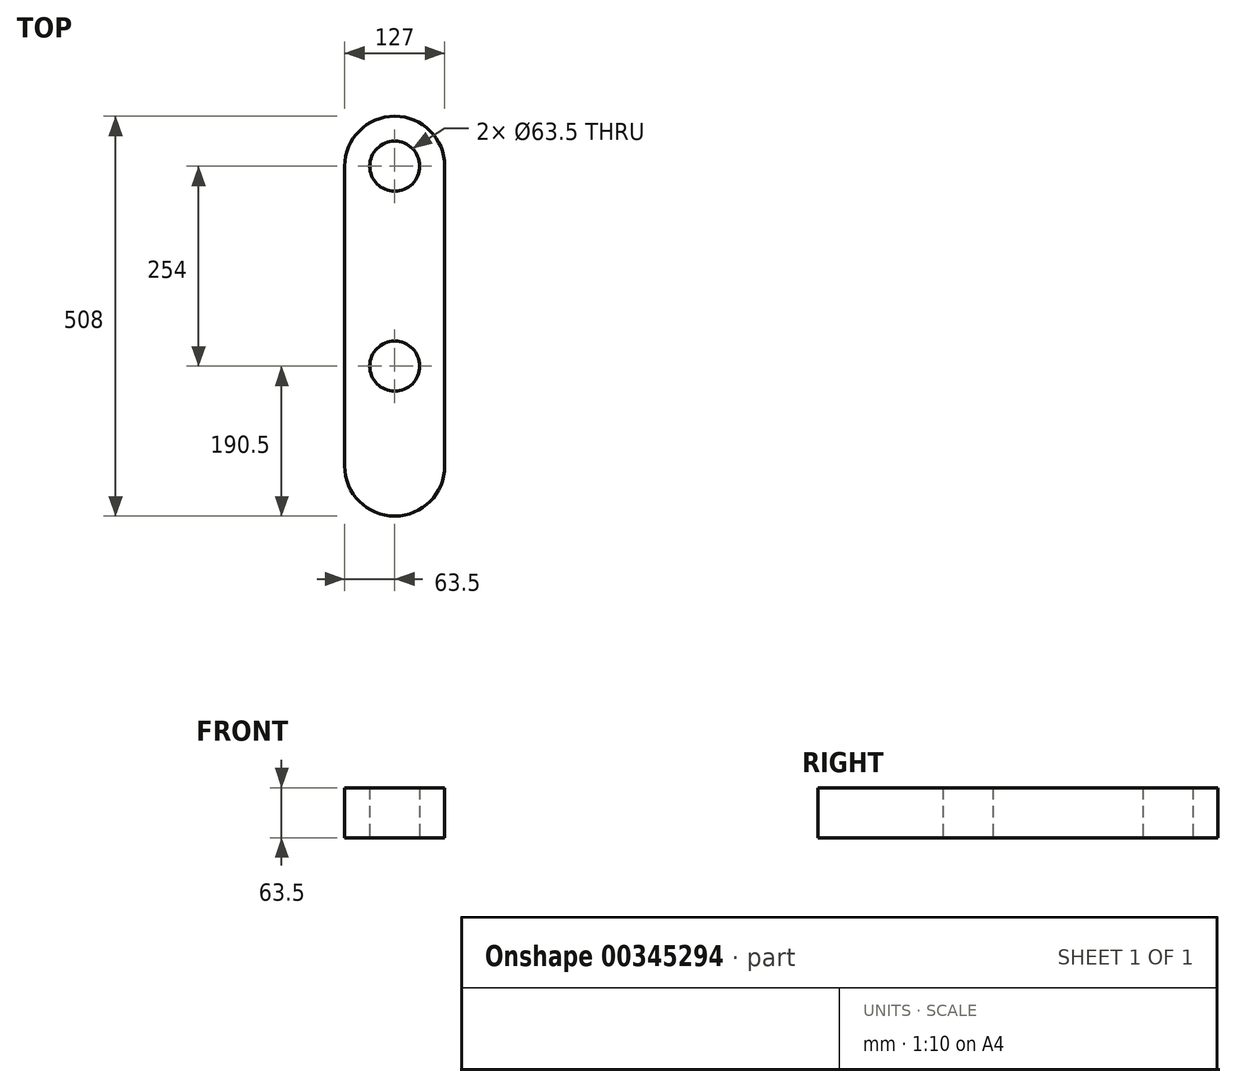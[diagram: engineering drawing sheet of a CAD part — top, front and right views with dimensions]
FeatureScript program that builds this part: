
annotation { "Feature Type Name" : "Feature", "Feature Type Description" : "" }
export const myFeature = defineFeature(function(context is Context, id is Id, definition is map)
    precondition{}
    {
        {
            var Q0;
            Q0=qCreatedBy(makeId("Top.planeOp"),FACE);
            var sketch = newSketch(context, id + "F0", { "sketchPlane" : qUnion([Q0])});
            skLineSegment(sketch, "E0.bottom", {"start": v(63.5, -190.5) * mm, "end": v(-63.5, -190.5) * mm});
            skLineSegment(sketch, "E0.top", {"start": v(63.5, 190.5) * mm, "end": v(-63.5, 190.5) * mm});
            skLineSegment(sketch, "E0.left", {"start": v(63.5, -190.5) * mm, "end": v(63.5, 190.5) * mm});
            skLineSegment(sketch, "E0.right", {"start": v(-63.5, -190.5) * mm, "end": v(-63.5, 190.5) * mm});
            skPoint(sketch, "E0.middle", {"position": v(0, 0) * mm});
            skCircle(sketch, "E1", {"center": v(0, 190.5) * mm, "radius": 63.5 * mm});
            skCircle(sketch, "E2", {"center": v(0, -190.5) * mm, "radius": 63.5 * mm});
            skSolve(sketch);
        }
        {
            var Q0;
            Q0=qSketchRegion(id+"F0",true);
            extrude(context, id + "F1", {"entities" : qUnion([Q0]), "depth" : 63.5 * mm});
        }
        {
            var Q0;
            Q0=qCreatedBy(makeId("Top.planeOp"),FACE);
            var sketch = newSketch(context, id + "F2", { "sketchPlane" : qUnion([Q0])});
            skCircle(sketch, "E3", {"center": v(0, 190.5) * mm, "radius": 31.75 * mm});
            skCircle(sketch, "E4", {"center": v(0, -63.5) * mm, "radius": 31.75 * mm});
            skSolve(sketch);
        }
        {
            var Q0;
            Q0=qSketchRegion(id+"F2",true);
            var Q1;
            Q1=makeQuery(id+"F1.opExtrude","SWEPT_BODY",BODY,{"disambiguationData":[OSD([sQuery(id+"F0.wireOp",EDGE,"E0.left"),sQuery(id+"F0.wireOp",EDGE,"E0.right"),sQuery(id+"F0.wireOp",EDGE,"E1"),sQuery(id+"F0.wireOp",EDGE,"E2")])]});
            extrude(context, id + "F3", {"entities" : qUnion([Q0]), "operationType" : NewBodyOperationType.REMOVE, "endBound" : BoundingType.UP_TO_BODY, "endBoundEntityBody" : qUnion([Q1]), "depth" : 25.4 * mm});
        }
    });
